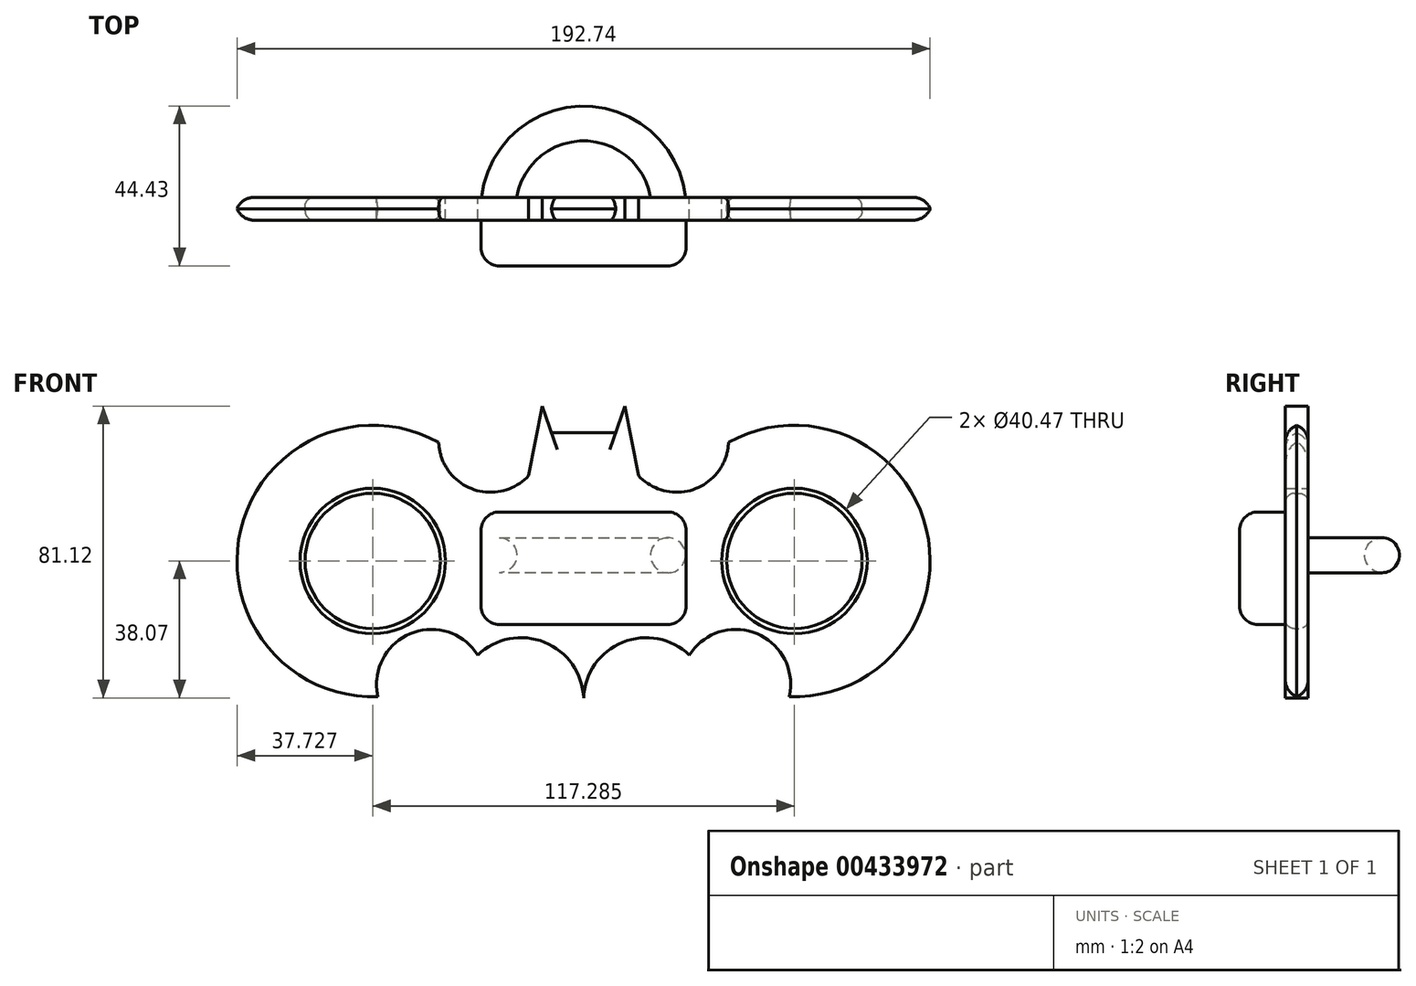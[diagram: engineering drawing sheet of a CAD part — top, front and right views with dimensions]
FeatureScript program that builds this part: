
annotation { "Feature Type Name" : "Feature", "Feature Type Description" : "" }
export const myFeature = defineFeature(function(context is Context, id is Id, definition is map)
    precondition{}
    {
        {
            var Q0;
            Q0=qCreatedBy(makeId("Front.planeOp"),FACE);
            var sketch = newSketch(context, id + "F0", { "sketchPlane" : qUnion([Q0])});
            skLineSegment(sketch, "E0", {"start": v(9.1, 34.46) * mm, "end": v(11.49, 41.44) * mm});
            skLineSegment(sketch, "E1", {"start": v(11.49, 41.44) * mm, "end": v(15.26, 22.13) * mm});
            skArc(sketch, "E2", {"start": v(15.26, 22.13) * mm, "mid": v(31.06, 18.44) * mm, "end": v(40.3, 31.79) * mm});
            skPoint(sketch, "E2.endSnap0", {"position": v(-13.17, 31.79) * mm});
            skArc(sketch, "E3", {"start": v(57.1, -39.68) * mm, "mid": v(95.73, 7.1) * mm, "end": v(40.3, 31.79) * mm});
            skArc(sketch, "E4", {"start": v(29.43, -27.76) * mm, "mid": v(10.86, -24.2) * mm, "end": v(0, -39.68) * mm});
            skArc(sketch, "E5", {"start": v(57.1, -39.68) * mm, "mid": v(48.37, -21.87) * mm, "end": v(29.43, -27.76) * mm});
            skLineSegment(sketch, "E6", {"start": v(0, 66.88) * mm, "end": v(0, -60.4) * mm, "construction": true});
            skLineSegment(sketch, "E7", {"start": v(0, 34.46) * mm, "end": v(9.1, 34.46) * mm});
            skLineSegment(sketch, "E8.MirrorCS", {"start": v(0, 34.46) * mm, "end": v(-9.1, 34.46) * mm});
            skLineSegment(sketch, "E9.MirrorCS", {"start": v(-9.1, 34.46) * mm, "end": v(-11.49, 41.44) * mm});
            skLineSegment(sketch, "E10.MirrorCS", {"start": v(-11.49, 41.44) * mm, "end": v(-15.26, 22.13) * mm});
            skArc(sketch, "E11.MirrorCS", {"start": v(-15.26, 22.13) * mm, "mid": v(-31.06, 18.44) * mm, "end": v(-40.3, 31.79) * mm});
            skArc(sketch, "E12.MirrorCS", {"start": v(-57.1, -39.68) * mm, "mid": v(-95.73, 7.1) * mm, "end": v(-40.3, 31.79) * mm});
            skArc(sketch, "E13.MirrorCS", {"start": v(-57.1, -39.68) * mm, "mid": v(-48.37, -21.87) * mm, "end": v(-29.43, -27.76) * mm});
            skArc(sketch, "E14.MirrorCS", {"start": v(-29.43, -27.76) * mm, "mid": v(-10.86, -24.2) * mm, "end": v(0, -39.68) * mm});
            skSolve(sketch);
        }
        {
            var Q0;
            Q0=makeQuery(id+"F0.imprint","IMPRINT",FACE,{"disambiguationData":[TD([[makeQuery(id+"F0.imprint","IMPRINT",EDGE,{"derivedFrom":sQuery(id+"F0.wireOp",EDGE,"E0")}),-1.0]])]});
            extrude(context, id + "F1", {"entities" : qUnion([Q0]), "endBound" : BoundingType.SYMMETRIC, "depth" : 6.35 * mm});
        }
        {
            var Q0;
            Q0=makeQuery(id+"F1.opExtrude","CAP_EDGE",EDGE,{"disambiguationData":[OSD([sQuery(id+"F0.wireOp",EDGE,"E12.MirrorCS")])],"isStart":false});
            var Q1;
            Q1=makeQuery(id+"F1.opExtrude","CAP_EDGE",EDGE,{"disambiguationData":[OSD([sQuery(id+"F0.wireOp",EDGE,"E12.MirrorCS")])],"isStart":true});
            var Q2;
            Q2=makeQuery(id+"F1.opExtrude","CAP_EDGE",EDGE,{"disambiguationData":[OSD([sQuery(id+"F0.wireOp",EDGE,"E3")])],"isStart":false});
            var Q3;
            Q3=makeQuery(id+"F1.opExtrude","CAP_EDGE",EDGE,{"disambiguationData":[OSD([sQuery(id+"F0.wireOp",EDGE,"E3")])],"isStart":true});
            var Q4;
            Q4=makeQuery(id+"F1.opExtrude","CAP_EDGE",EDGE,{"disambiguationData":[OSD([sQuery(id+"F0.wireOp",EDGE,"E7"),sQuery(id+"F0.wireOp",EDGE,"E8.MirrorCS")])],"isStart":false});
            var Q5;
            Q5=makeQuery(id+"F1.opExtrude","CAP_EDGE",EDGE,{"disambiguationData":[OSD([sQuery(id+"F0.wireOp",EDGE,"E7"),sQuery(id+"F0.wireOp",EDGE,"E8.MirrorCS")])],"isStart":true});
            fillet(context, id + "F2", {"entities" : qUnion([Q0, Q1, Q2, Q3, Q4, Q5]), "radius" : 5.08 * mm, "tangentPropagation" : true, "allowEdgeOverflow" : false});
        }
        {
            var Q0;
            Q0=makeQuery(id+"F1.opExtrude","CAP_FACE",FACE,{"disambiguationData":[OSD([sQuery(id+"F0.wireOp",EDGE,"E0"),sQuery(id+"F0.wireOp",EDGE,"E1"),sQuery(id+"F0.wireOp",EDGE,"E2"),sQuery(id+"F0.wireOp",EDGE,"E3"),sQuery(id+"F0.wireOp",EDGE,"E4"),sQuery(id+"F0.wireOp",EDGE,"E5"),sQuery(id+"F0.wireOp",EDGE,"E7"),sQuery(id+"F0.wireOp",EDGE,"E8.MirrorCS"),sQuery(id+"F0.wireOp",EDGE,"E9.MirrorCS"),sQuery(id+"F0.wireOp",EDGE,"E10.MirrorCS"),sQuery(id+"F0.wireOp",EDGE,"E11.MirrorCS"),sQuery(id+"F0.wireOp",EDGE,"E12.MirrorCS"),sQuery(id+"F0.wireOp",EDGE,"E13.MirrorCS"),sQuery(id+"F0.wireOp",EDGE,"E14.MirrorCS")])],"isStart":true});
            var sketch = newSketch(context, id + "F3", { "sketchPlane" : qUnion([Q0])});
            skCircle(sketch, "E15", {"center": v(-58.64, -1.61) * mm, "radius": 20.24 * mm});
            skCircle(sketch, "E16.MirrorC", {"center": v(58.64, -1.61) * mm, "radius": 20.24 * mm});
            skCircle(sketch, "E17", {"center": v(-58.64, -1.61) * mm, "radius": 18.81 * mm});
            skCircle(sketch, "E18.MirrorC", {"center": v(58.64, -1.61) * mm, "radius": 18.81 * mm});
            skSolve(sketch);
        }
        {
            var Q0;
            Q0 = qSketchRegion(id + "F3", true);
            extrude(context, id + "F4", {"entities" : qUnion([Q0]), "operationType" : NewBodyOperationType.REMOVE, "endBound" : BoundingType.THROUGH_ALL, "oppositeDirection" : true, "depth" : 25.4 * mm});
        }
        {
            var Q0;
            Q0=makeQuery(id+"F4.boolean.opBoolean","COPY",EDGE,{"derivedFrom":makeQuery(id+"F4.opExtrude","CAP_EDGE",EDGE,{"disambiguationData":[OSD([sQuery(id+"F3.wireOp",EDGE,"E17")])],"isStart":true})});
            var Q1;
            Q1=makeQuery(id+"F4.boolean.opBoolean","COPY",EDGE,{"derivedFrom":makeQuery(id+"F4.opExtrude","CAP_EDGE",EDGE,{"disambiguationData":[OSD([sQuery(id+"F3.wireOp",EDGE,"E18.MirrorC")])],"isStart":true})});
            var Q2;
            Q2=makeQuery(id+"F4.boolean.opBoolean","INTERSECT",EDGE,{"derivedFrom":[makeQuery(id+"F1.opExtrude","CAP_FACE",FACE,{"disambiguationData":[OSD([sQuery(id+"F0.wireOp",EDGE,"E0"),sQuery(id+"F0.wireOp",EDGE,"E1"),sQuery(id+"F0.wireOp",EDGE,"E2"),sQuery(id+"F0.wireOp",EDGE,"E3"),sQuery(id+"F0.wireOp",EDGE,"E4"),sQuery(id+"F0.wireOp",EDGE,"E5"),sQuery(id+"F0.wireOp",EDGE,"E7"),sQuery(id+"F0.wireOp",EDGE,"E8.MirrorCS"),sQuery(id+"F0.wireOp",EDGE,"E9.MirrorCS"),sQuery(id+"F0.wireOp",EDGE,"E10.MirrorCS"),sQuery(id+"F0.wireOp",EDGE,"E11.MirrorCS"),sQuery(id+"F0.wireOp",EDGE,"E12.MirrorCS"),sQuery(id+"F0.wireOp",EDGE,"E13.MirrorCS"),sQuery(id+"F0.wireOp",EDGE,"E14.MirrorCS")])],"isStart":false}),makeQuery(id+"F4.opExtrude","SWEPT_FACE",FACE,{"disambiguationData":[OSD([sQuery(id+"F3.wireOp",EDGE,"E17")])]})]});
            var Q3;
            Q3=makeQuery(id+"F4.boolean.opBoolean","INTERSECT",EDGE,{"derivedFrom":[makeQuery(id+"F1.opExtrude","CAP_FACE",FACE,{"disambiguationData":[OSD([sQuery(id+"F0.wireOp",EDGE,"E0"),sQuery(id+"F0.wireOp",EDGE,"E1"),sQuery(id+"F0.wireOp",EDGE,"E2"),sQuery(id+"F0.wireOp",EDGE,"E3"),sQuery(id+"F0.wireOp",EDGE,"E4"),sQuery(id+"F0.wireOp",EDGE,"E5"),sQuery(id+"F0.wireOp",EDGE,"E7"),sQuery(id+"F0.wireOp",EDGE,"E8.MirrorCS"),sQuery(id+"F0.wireOp",EDGE,"E9.MirrorCS"),sQuery(id+"F0.wireOp",EDGE,"E10.MirrorCS"),sQuery(id+"F0.wireOp",EDGE,"E11.MirrorCS"),sQuery(id+"F0.wireOp",EDGE,"E12.MirrorCS"),sQuery(id+"F0.wireOp",EDGE,"E13.MirrorCS"),sQuery(id+"F0.wireOp",EDGE,"E14.MirrorCS")])],"isStart":false}),makeQuery(id+"F4.opExtrude","SWEPT_FACE",FACE,{"disambiguationData":[OSD([sQuery(id+"F3.wireOp",EDGE,"E18.MirrorC")])]})]});
            fillet(context, id + "F5", {"entities" : qUnion([Q0, Q1, Q2, Q3]), "radius" : 2.54 * mm, "tangentPropagation" : true, "allowEdgeOverflow" : false});
        }
        {
            var Q0;
            {var subQ0=sQuery(id+"F0.wireOp",EDGE,"E13.MirrorCS");var subQ1=sQuery(id+"F0.wireOp",EDGE,"E10.MirrorCS");var subQ2=sQuery(id+"F0.wireOp",EDGE,"E3");var subQ3=sQuery(id+"F0.wireOp",EDGE,"E9.MirrorCS");var subQ4=sQuery(id+"F0.wireOp",EDGE,"E5");var subQ5=sQuery(id+"F0.wireOp",EDGE,"E11.MirrorCS");var subQ6=sQuery(id+"F0.wireOp",EDGE,"E0");var subQ7=sQuery(id+"F0.wireOp",EDGE,"E14.MirrorCS");var subQ8=sQuery(id+"F0.wireOp",EDGE,"E12.MirrorCS");var subQ9=sQuery(id+"F0.wireOp",EDGE,"E1");var subQ10=sQuery(id+"F0.wireOp",EDGE,"E2");var subQ11=sQuery(id+"F0.wireOp",EDGE,"E4");var subQ12=sQuery(id+"F0.wireOp",EDGE,"E8.MirrorCS");var subQ13=sQuery(id+"F0.wireOp",EDGE,"E7");Q0=makeQuery(id+"F4.boolean.opBoolean","SPLIT",FACE,{"disambiguationData":[TD([makeQuery(id+"F1.opExtrude","SWEPT_FACE",FACE,{"disambiguationData":[OSD([subQ6])]})])],"derivedFrom":makeQuery(id+"F1.opExtrude","CAP_FACE",FACE,{"disambiguationData":[OSD([subQ6,subQ9,subQ10,subQ2,subQ11,subQ4,subQ13,subQ12,subQ3,subQ1,subQ5,subQ8,subQ0,subQ7])],"isStart":false})});}
            var sketch = newSketch(context, id + "F6", { "sketchPlane" : qUnion([Q0])});
            skPoint(sketch, "E19.middle", {"position": v(0, 0) * mm});
            skLineSegment(sketch, "E20.top", {"start": v(0, -19.28) * mm, "end": v(28.49, -19.28) * mm});
            skLineSegment(sketch, "E20.right", {"start": v(28.49, 0) * mm, "end": v(28.49, -19.28) * mm});
            skLineSegment(sketch, "E21.top", {"start": v(0, 12) * mm, "end": v(28.49, 12) * mm});
            skLineSegment(sketch, "E21.right", {"start": v(28.49, 0) * mm, "end": v(28.49, 12) * mm});
            skLineSegment(sketch, "E22.MirrorCS", {"start": v(0, 12) * mm, "end": v(-28.49, 12) * mm});
            skLineSegment(sketch, "E23.MirrorCS", {"start": v(-28.49, 0) * mm, "end": v(-28.49, 12) * mm});
            skLineSegment(sketch, "E24.MirrorCS", {"start": v(-28.49, 0) * mm, "end": v(-28.49, -19.28) * mm});
            skLineSegment(sketch, "E25.MirrorCS", {"start": v(0, -19.28) * mm, "end": v(-28.49, -19.28) * mm});
            skSolve(sketch);
        }
        {
            var Q0;
            Q0 = qSketchRegion(id + "F6", true);
            extrude(context, id + "F7", {"entities" : qUnion([Q0]), "operationType" : NewBodyOperationType.ADD, "depth" : 12.7 * mm});
        }
        {
            var Q0;
            Q0=makeQuery(id+"F7.opExtrude","CAP_EDGE",EDGE,{"disambiguationData":[OSD([sQuery(id+"F6.wireOp",EDGE,"E21.top"),sQuery(id+"F6.wireOp",EDGE,"E22.MirrorCS")])],"isStart":false});
            var Q1;
            Q1=makeQuery(id+"F7.opExtrude","CAP_EDGE",EDGE,{"disambiguationData":[OSD([sQuery(id+"F6.wireOp",EDGE,"E23.MirrorCS"),sQuery(id+"F6.wireOp",EDGE,"E24.MirrorCS")])],"isStart":false});
            var Q2;
            Q2=makeQuery(id+"F7.opExtrude","CAP_EDGE",EDGE,{"disambiguationData":[OSD([sQuery(id+"F6.wireOp",EDGE,"E20.right"),sQuery(id+"F6.wireOp",EDGE,"E21.right")])],"isStart":false});
            var Q3;
            Q3=makeQuery(id+"F7.opExtrude","SWEPT_EDGE",EDGE,{"disambiguationData":[OSD([sQuery(id+"F6.wireOp",EDGE,"E21.top"),sQuery(id+"F6.wireOp",EDGE,"E21.right")])]});
            var Q4;
            Q4=makeQuery(id+"F7.opExtrude","SWEPT_EDGE",EDGE,{"disambiguationData":[OSD([sQuery(id+"F6.wireOp",EDGE,"E22.MirrorCS"),sQuery(id+"F6.wireOp",EDGE,"E23.MirrorCS")])]});
            var Q5;
            Q5=makeQuery(id+"F7.opExtrude","SWEPT_EDGE",EDGE,{"disambiguationData":[OSD([sQuery(id+"F6.wireOp",EDGE,"E20.top"),sQuery(id+"F6.wireOp",EDGE,"E20.right")])]});
            var Q6;
            Q6=makeQuery(id+"F7.opExtrude","CAP_EDGE",EDGE,{"disambiguationData":[OSD([sQuery(id+"F6.wireOp",EDGE,"E20.top"),sQuery(id+"F6.wireOp",EDGE,"E25.MirrorCS")])],"isStart":false});
            var Q7;
            Q7=makeQuery(id+"F7.opExtrude","SWEPT_EDGE",EDGE,{"disambiguationData":[OSD([sQuery(id+"F6.wireOp",EDGE,"E24.MirrorCS"),sQuery(id+"F6.wireOp",EDGE,"E25.MirrorCS")])]});
            fillet(context, id + "F8", {"entities" : qUnion([Q0, Q1, Q2, Q3, Q4, Q5, Q6, Q7]), "radius" : 5.08 * mm, "tangentPropagation" : true, "allowEdgeOverflow" : false});
        }
        {
            var Q0;
            Q0=makeQuery(id+"F3.imprint","IMPRINT",FACE,{"disambiguationData":[TD([[makeQuery(id+"F3.imprint","IMPRINT",EDGE,{"derivedFrom":sQuery(id+"F3.wireOp",EDGE,"E15")}),-1.0]])]});
            var sketch = newSketch(context, id + "F9", { "sketchPlane" : qUnion([Q0])});
            skCircle(sketch, "E26", {"center": v(-23.5, 0) * mm, "radius": 4.87 * mm});
            skCircle(sketch, "E27.MirrorC", {"center": v(23.5, 0) * mm, "radius": 4.87 * mm});
            skSolve(sketch);
        }
        {
            var Q0;
            Q0=makeQuery(id+"F9.imprint","IMPRINT",FACE,{"disambiguationData":[TD([[makeQuery(id+"F9.imprint","IMPRINT",EDGE,{"derivedFrom":sQuery(id+"F9.wireOp",EDGE,"E26")}),1.0]])]});
            var Q1;
            Q1=sQuery(id+"F0.wireOp",EDGE,"E6");
            revolve(context, id + "F10", {"operationType" : NewBodyOperationType.ADD, "entities" : qUnion([Q0]), "axis" : qUnion([Q1]), "revolveType" : RevolveType.ONE_DIRECTION, "oppositeDirection" : true, "angle" : 177.76 * degree});
        }
    });
